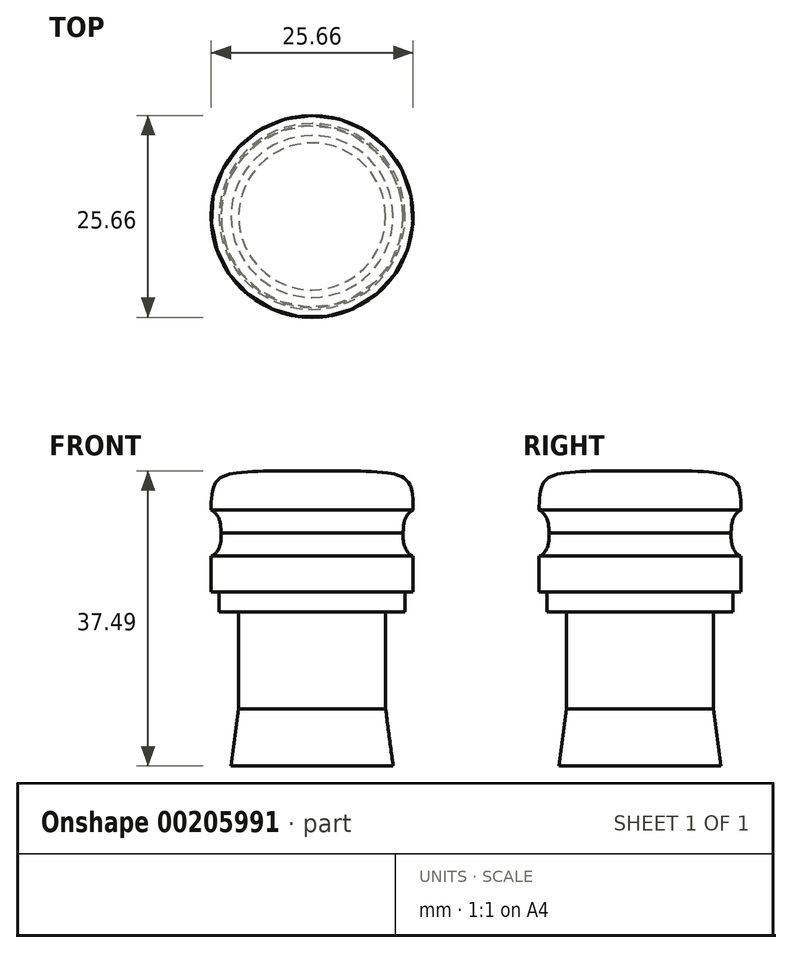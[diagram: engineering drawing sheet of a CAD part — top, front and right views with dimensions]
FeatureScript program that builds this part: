
annotation { "Feature Type Name" : "Feature", "Feature Type Description" : "" }
export const myFeature = defineFeature(function(context is Context, id is Id, definition is map)
    precondition{}
    {
        {
            var Q0;
            Q0=qCreatedBy(makeId("Right.planeOp"),FACE);
            var sketch = newSketch(context, id + "F0", { "sketchPlane" : qUnion([Q0])});
            skLineSegment(sketch, "E0", {"start": v(0, 0) * mm, "end": v(10.29, 0) * mm});
            skLineSegment(sketch, "E1", {"start": v(10.29, 0) * mm, "end": v(9.33, 7.24) * mm});
            skLineSegment(sketch, "E2", {"start": v(9.33, 7.24) * mm, "end": v(9.33, 19.56) * mm});
            skLineSegment(sketch, "E3", {"start": v(9.33, 19.56) * mm, "end": v(11.81, 19.56) * mm});
            skLineSegment(sketch, "E4", {"start": v(11.81, 19.56) * mm, "end": v(11.81, 22.1) * mm});
            skLineSegment(sketch, "E5", {"start": v(11.81, 22.1) * mm, "end": v(12.83, 22.1) * mm});
            skLineSegment(sketch, "E6", {"start": v(12.83, 22.1) * mm, "end": v(12.83, 26.67) * mm});
            skLineSegment(sketch, "E7", {"start": v(12.83, 26.67) * mm, "end": v(12.83, 32.51) * mm, "construction": true});
            skLineSegment(sketch, "E8", {"start": v(12.83, 32.51) * mm, "end": v(12.83, 37.47) * mm, "construction": true});
            skLineSegment(sketch, "E9", {"start": v(12.83, 37.47) * mm, "end": v(0, 37.47) * mm, "construction": true});
            skLineSegment(sketch, "E10", {"start": v(0, 37.46) * mm, "end": v(0, 0) * mm});
            skFitSpline(sketch, "E11", {"points": [v(0, 37.47) * mm, v(10.08, 37.16) * mm, v(12.24, 36.01) * mm, v(12.83, 32.51) * mm], "startDerivative": vector(18.54, 0) * mm, "endDerivative": vector(0, -19.7) * mm});
            skPoint(sketch, "E12", {"position": v(12.83, 29.6) * mm});
            skLineSegment(sketch, "E13", {"start": v(12.83, 29.6) * mm, "end": v(11.56, 29.6) * mm, "construction": true});
            skPoint(sketch, "E14", {"position": v(8.35, 29.6) * mm});
            skLineSegment(sketch, "E15", {"start": v(11.56, 29.6) * mm, "end": v(0, 29.6) * mm, "construction": true});
            skFitSpline(sketch, "E16", {"points": [v(12.83, 32.51) * mm, v(11.89, 31.55) * mm, v(11.56, 29.6) * mm], "startDerivative": vector(-2.46, -0.69) * mm, "endDerivative": vector(-0.25, -4.83) * mm});
            skFitSpline(sketch, "E17", {"points": [v(12.83, 26.67) * mm, v(11.87, 27.6) * mm, v(11.56, 29.6) * mm], "startDerivative": vector(-2.8, 0.55) * mm, "endDerivative": vector(0.05, 4.98) * mm});
            skSolve(sketch);
        }
        {
            var Q0;
            Q0=makeQuery(id+"F0.imprint","IMPRINT",FACE,{"disambiguationData":[TD([[makeQuery(id+"F0.imprint","IMPRINT",EDGE,{"derivedFrom":sQuery(id+"F0.wireOp",EDGE,"E0")}),1.0]])]});
            var Q1;
            Q1=sQuery(id+"F0.wireOp",EDGE,"E10");
            revolve(context, id + "F1", {"entities" : qUnion([Q0]), "axis" : qUnion([Q1]), "revolveType" : RevolveType.FULL});
        }
    });
